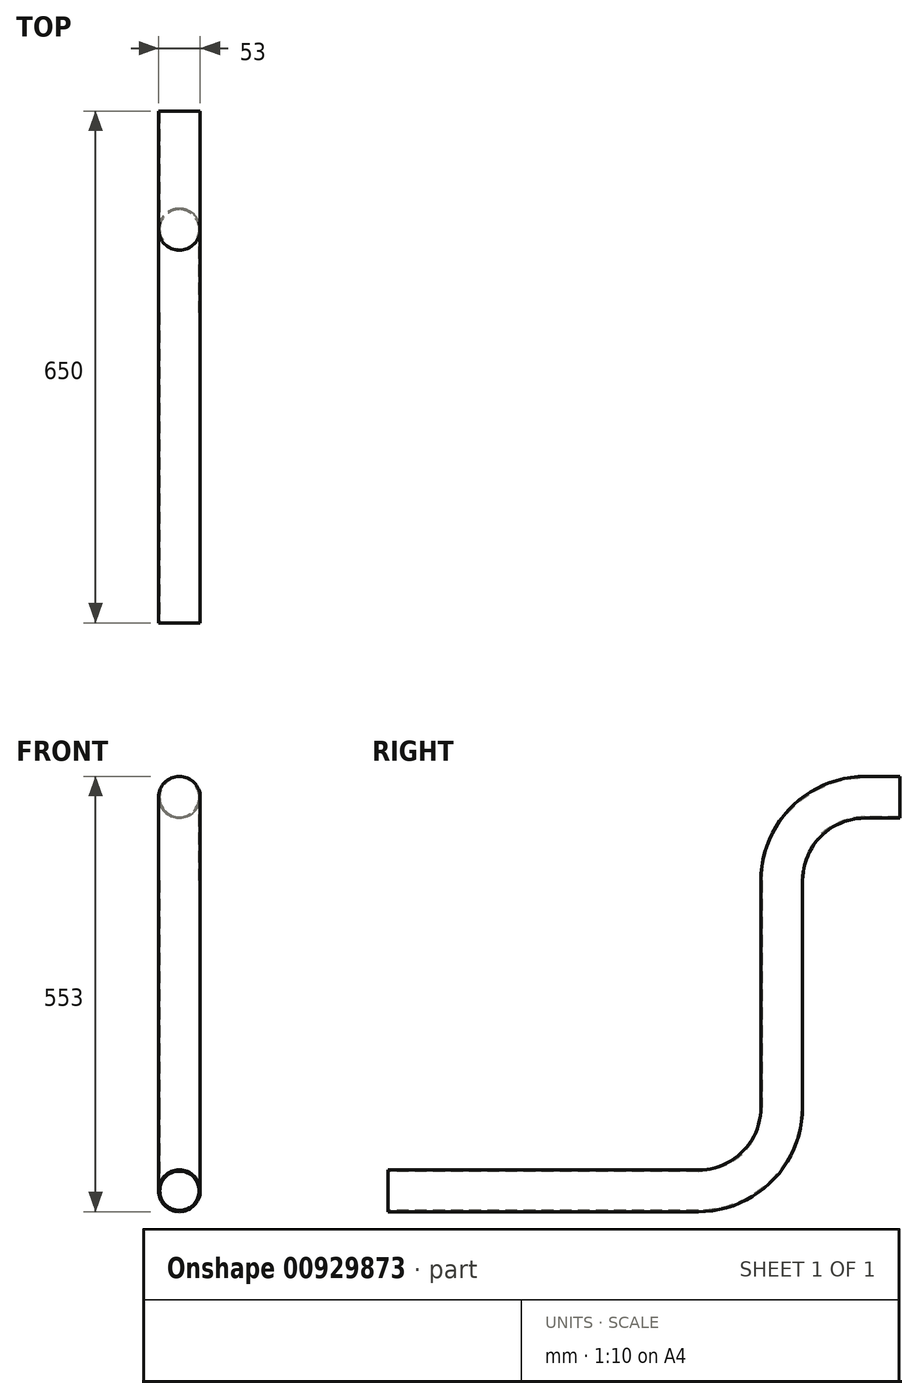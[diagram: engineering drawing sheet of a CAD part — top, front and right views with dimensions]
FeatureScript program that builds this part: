
annotation { "Feature Type Name" : "Feature", "Feature Type Description" : "" }
export const myFeature = defineFeature(function(context is Context, id is Id, definition is map)
    precondition{}
    {
        {
            var Q0;
            Q0=qCreatedBy(makeId("Front.planeOp"),FACE);
            var sketch = newSketch(context, id + "F0", { "sketchPlane" : qUnion([Q0])});
            skCircle(sketch, "E0", {"center": v(0, 0) * mm, "radius": 26.5 * mm});
            skCircle(sketch, "E1", {"center": v(0, 0) * mm, "radius": 25 * mm});
            skSolve(sketch);
        }
        {
            var Q0;
            Q0=qCreatedBy(makeId("Right.planeOp"),FACE);
            var sketch = newSketch(context, id + "F1", { "sketchPlane" : qUnion([Q0])});
            skLineSegment(sketch, "E2", {"start": v(0, 0) * mm, "end": v(-44, 0) * mm});
            skLineSegment(sketch, "E3", {"start": v(-150, -106) * mm, "end": v(-150, -394) * mm});
            skLineSegment(sketch, "E4", {"start": v(-256, -500) * mm, "end": v(-650, -500) * mm});
            skPoint(sketch, "E5.visualSharp", {"position": v(-150, 0) * mm});
            skArc(sketch, "E5.filletArc", {"start": v(-44, 0) * mm, "mid": v(-118.95, -31.05) * mm, "end": v(-150, -106) * mm});
            skPoint(sketch, "E6.visualSharp", {"position": v(-150, -500) * mm});
            skArc(sketch, "E6.filletArc", {"start": v(-256, -500) * mm, "mid": v(-181.05, -468.95) * mm, "end": v(-150, -394) * mm});
            skSolve(sketch);
        }
        {
            var Q0;
            Q0=makeQuery(id+"F0.imprint","IMPRINT",FACE,{"disambiguationData":[TD([[makeQuery(id+"F0.imprint","IMPRINT",EDGE,{"derivedFrom":sQuery(id+"F0.wireOp",EDGE,"E0")}),1.0]])]});
            var Q1;
            Q1=sQuery(id+"F1.wireOp",EDGE,"E2");
            var Q2;
            Q2=sQuery(id+"F1.wireOp",EDGE,"E5.filletArc");
            var Q3;
            Q3=sQuery(id+"F1.wireOp",EDGE,"E3");
            var Q4;
            Q4=sQuery(id+"F1.wireOp",EDGE,"E6.filletArc");
            var Q5;
            Q5=sQuery(id+"F1.wireOp",EDGE,"E4");
            sweep(context, id + "F2", {"profiles" : qUnion([Q0]), "path" : qUnion([Q1, Q2, Q3, Q4, Q5])});
        }
    });
